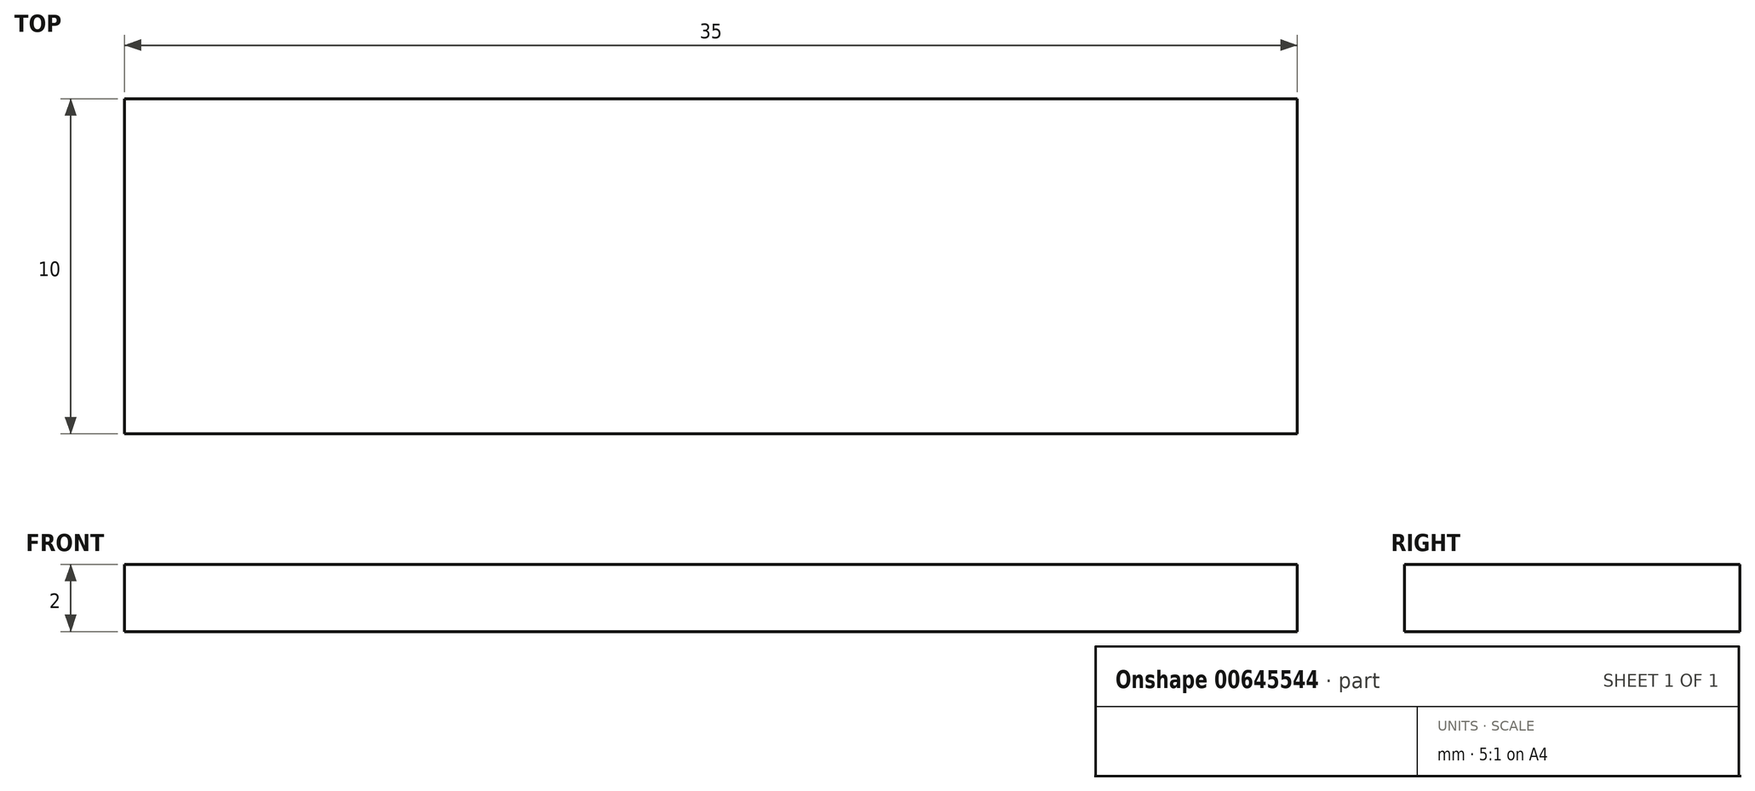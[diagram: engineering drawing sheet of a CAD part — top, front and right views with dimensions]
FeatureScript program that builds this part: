
annotation { "Feature Type Name" : "Feature", "Feature Type Description" : "" }
export const myFeature = defineFeature(function(context is Context, id is Id, definition is map)
    precondition{}
    {
        {
            var Q0;
            Q0=qCreatedBy(makeId("Top.planeOp"),FACE);
            var sketch = newSketch(context, id + "F0", { "sketchPlane" : qUnion([Q0])});
            skLineSegment(sketch, "E0.bottom", {"start": v(-17.5, 5) * mm, "end": v(17.5, 5) * mm});
            skLineSegment(sketch, "E0.top", {"start": v(-17.5, -5) * mm, "end": v(17.5, -5) * mm});
            skLineSegment(sketch, "E0.left", {"start": v(-17.5, 5) * mm, "end": v(-17.5, -5) * mm});
            skLineSegment(sketch, "E0.right", {"start": v(17.5, 5) * mm, "end": v(17.5, -5) * mm});
            skPoint(sketch, "E0.middle", {"position": v(0, 0) * mm});
            skSolve(sketch);
        }
        {
            var Q0;
            Q0=qSketchRegion(id+"F0",true);
            extrude(context, id + "F1", {"entities" : qUnion([Q0]), "depth" : 2 * mm, "offsetDistance" : 25 * mm});
        }
    });
